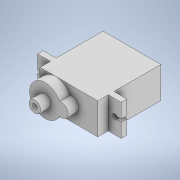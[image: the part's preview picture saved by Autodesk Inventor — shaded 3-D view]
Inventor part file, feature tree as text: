
AUTODESK INVENTOR PART (.ipt)
format: ipt  version: 2021 (Build 250183000, 183)  size: 190,464 bytes
history: native  units: mm
features: sketch x9, extrude x7, hole x2
ambient origin geometry x8: Origin, YZ Plane, XZ Plane, XY Plane, X Axis, Y Axis, Z Axis, Center Point
bodies: Solid1 (feature_tree)
feature tree (18):
  extrude  "Extrusion1"  Depth=12.0mm
  extrude  "Extrusion2"  Depth=6.0mm
  extrude  "Extrusion3"  Depth=5.0mm
  extrude  "Extrusion4"  Depth=2.2mm TaperAngle=0.0deg
  extrude  "Extrusion5"  Depth=5.0mm
  extrude  "Extrusion6"  Depth=6.0mm
  hole  "Hole1"  [1 undecoded]
  hole  "Hole2"  [1 undecoded]
  extrude  "Extrusion7"  Depth=4.0mm TaperAngle=0.0deg
  sketch  "Sketch1"  dims[d0=22.2mm d1=12.0mm]
  sketch  "Sketch2"  dims[d2=6.0mm d3=11.1mm]
  sketch  "Sketch3"  dims[d4=18.0mm d5=0.0mm d6=5.0mm]
  sketch  "Sketch4"  dims[d7=5.0mm d8=2.2mm d9=0.0mm]
  sketch  "Sketch5"  dims[d10=5.0mm d11=5.0mm]
  sketch  "Sketch6"  dims[d12=4.0mm d13=0.0mm d14=6.0mm]
  sketch  "Sketch7"  dims[d15=4.0mm d16=0.0mm d17=5.2mm]
  sketch  "Sketch8"  dims[d18=10.0mm d19=4.0mm d20=0.0mm]
  sketch  "Sketch9"  dims[d21=4.4mm d22=4.0mm d23=0.0mm d24=2.0mm d25=6.0mm d26=4.0mm d27=2.0mm d28=90.0deg d29=4.0mm d30=20.594885mm d31=2.5mm d32=2.5mm d33=2.0mm d34=6.0mm d35=4.0mm d36=2.0mm d37=90.0deg d38=4.0mm d39=20.594885mm d40=1.0mm d41=0.5mm d42=1.0mm d43=0.5mm d44=4.0mm d45=0.0mm]
note: 2 required parameter values undecoded (feature->parameter linkage not recoverable at this tier; creation-order binding heuristic only, values carry confidence <= 0.55)
